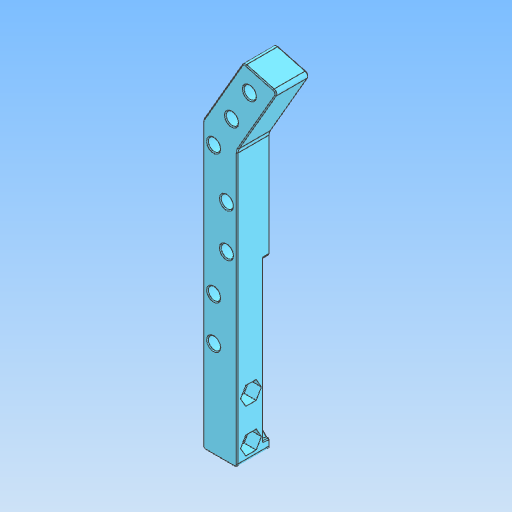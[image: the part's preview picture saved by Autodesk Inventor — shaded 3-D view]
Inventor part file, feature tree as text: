
AUTODESK INVENTOR PART (.ipt)
format: ipt  version: 2021.2 (Build 252289000, 289)  size: 471,040 bytes
history: native  units: mm
features: other x6, fillet x3, chamfer x3
ambient origin geometry x8: Origin, YZ Plane, XZ Plane, XY Plane, X Axis, Y Axis, Z Axis, Center Point
bodies: Body1 (feature_tree)
feature tree (12):
  other  "Твёрдое тело.ipt"
  other  "Непосредственное редактирование1"
  fillet  "Сопряжение1"  Radius=10.0mm
  chamfer  "Фаска1"  [1 undecoded]
  chamfer  "Фаска2"  Distance=5.0mm
  fillet  "Сопряжение2"  Radius=2.0mm
  fillet  "Сопряжение3"  Radius=0.5mm
  chamfer  "Фаска3"  Distance=0.5mm Angle=45.0deg
  other  "Ножка правая низ::Твёрдое тело.ipt"
  other  "Элемент создания тегов1"
  other  "Твердое тело1"
  other  "Перенос1"
note: 1 required parameter value undecoded (feature->parameter linkage not recoverable at this tier; creation-order binding heuristic only, values carry confidence <= 0.55)
